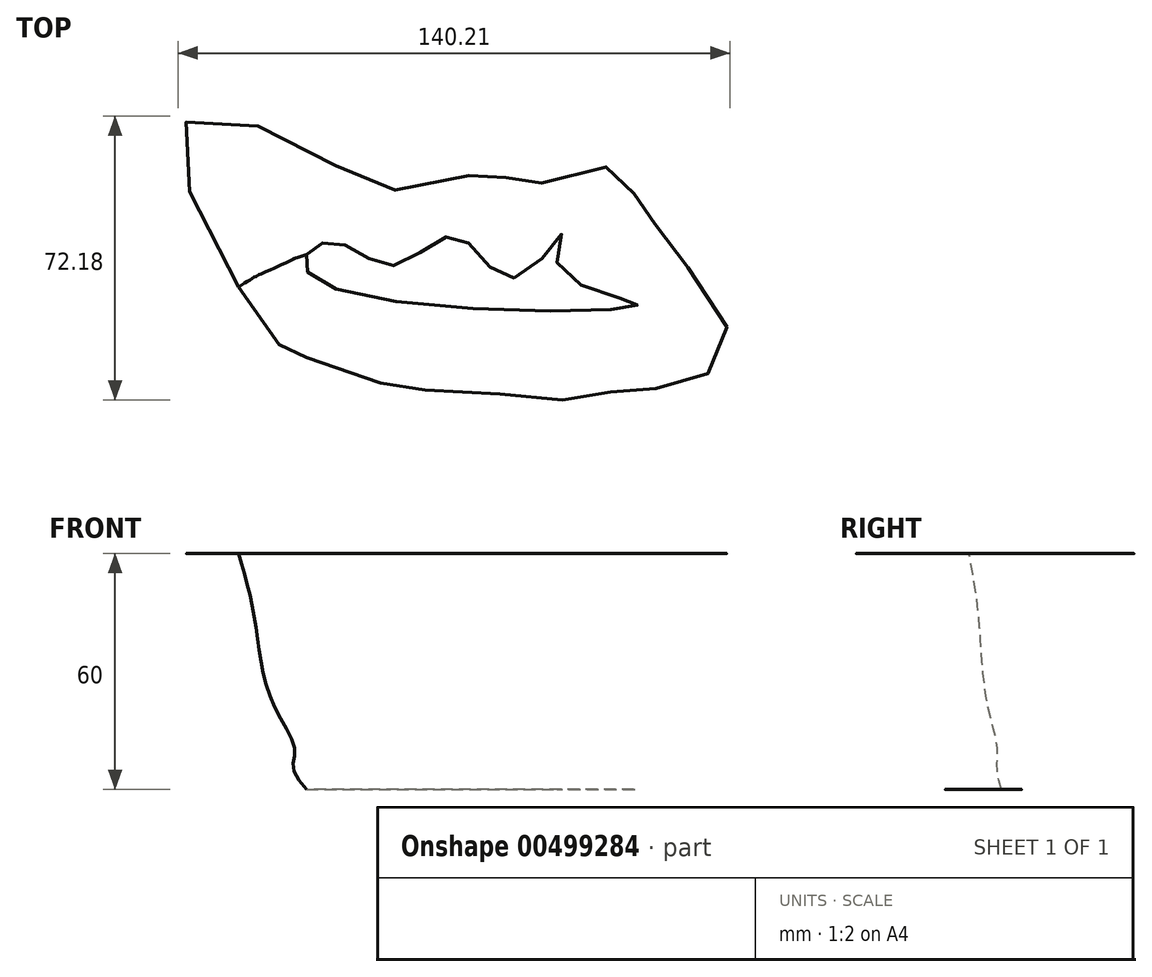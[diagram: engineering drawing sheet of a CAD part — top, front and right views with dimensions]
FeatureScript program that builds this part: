
annotation { "Feature Type Name" : "Feature", "Feature Type Description" : "" }
export const myFeature = defineFeature(function(context is Context, id is Id, definition is map)
    precondition{}
    {
        {
            var Q0;
            Q0=qCreatedBy(makeId("Top.planeOp"),FACE);
            var sketch = newSketch(context, id + "F0", { "sketchPlane" : qUnion([Q0])});
            skFitSpline(sketch, "E0", {"points": [v(-38.2, 16.28) * mm, v(-29.92, 19.29) * mm, v(-16, 13.45) * mm, v(0, 20.98) * mm, v(13.92, 10.26) * mm, v(27.28, 22.3) * mm, v(25.97, 12.89) * mm, v(45.91, 3.48) * mm, v(-31.61, 7.8) * mm, v(-38.2, 16.28) * mm]});
            skSolve(sketch);
        }
        {
            var Q0;
            Q0=makeQuery(id+"F0.imprint","IMPRINT",FACE,{"disambiguationData":[TD([[makeQuery(id+"F0.imprint","IMPRINT",EDGE,{"derivedFrom":sQuery(id+"F0.wireOp",EDGE,"E0")}),-1.0]])]});
            cPlane(context, id + "F1", {"entities" : qUnion([Q0]), "cplaneType" : CPlaneType.OFFSET, "offset" : 5 * mm, "width" : 150 * mm, "height" : 150 * mm});
        }
        {
            var Q0;
            Q0=qCreatedBy(id+"F1.planeOp",FACE);
            var sketch = newSketch(context, id + "F2", { "sketchPlane" : qUnion([Q0])});
            skFitSpline(sketch, "E1", {"points": [v(48.17, 4.42) * mm, v(30.67, 11) * mm, v(32.74, 26.25) * mm, v(14.3, 14.2) * mm, v(4.33, 24.18) * mm, v(-11.3, 21.17) * mm, v(-19.2, 16.84) * mm, v(-35, 23.24) * mm, v(-41.96, 17.6) * mm, v(-33.5, 3.86) * mm, v(-30.48, 3.3) * mm, v(41.59, -2.54) * mm, v(48.17, 4.42) * mm]});
            skSolve(sketch);
        }
        {
            var Q0;
            Q0=makeQuery(id+"F2.imprint","IMPRINT",FACE,{"disambiguationData":[TD([[makeQuery(id+"F2.imprint","IMPRINT",EDGE,{"derivedFrom":sQuery(id+"F2.wireOp",EDGE,"E1")}),1.0]])]});
            cPlane(context, id + "F3", {"entities" : qUnion([Q0]), "cplaneType" : CPlaneType.OFFSET, "offset" : 5 * mm, "width" : 150 * mm, "height" : 150 * mm});
        }
        {
            var Q0;
            Q0=qCreatedBy(id+"F3.planeOp",FACE);
            var sketch = newSketch(context, id + "F4", { "sketchPlane" : qUnion([Q0])});
            skFitSpline(sketch, "E2", {"points": [v(-33.3, 4.23) * mm, v(-41.2, 18.53) * mm, v(-29.17, 21.73) * mm, v(-17.69, 16.84) * mm, v(4.14, 18.91) * mm, v(14.11, 12.14) * mm, v(30.48, 21.92) * mm, v(29.35, 11.38) * mm, v(46.1, 4.8) * mm, v(31.42, -5.74) * mm, v(-25.4, 1.79) * mm, v(-33.3, 4.23) * mm]});
            skSolve(sketch);
        }
        {
            var Q0;
            Q0=makeQuery(id+"F4.imprint","IMPRINT",FACE,{"disambiguationData":[TD([[makeQuery(id+"F4.imprint","IMPRINT",EDGE,{"derivedFrom":sQuery(id+"F4.wireOp",EDGE,"E2")}),-1.0]])]});
            cPlane(context, id + "F5", {"entities" : qUnion([Q0]), "cplaneType" : CPlaneType.OFFSET, "offset" : 10 * mm, "width" : 150 * mm, "height" : 150 * mm});
        }
        {
            var Q0;
            Q0=qCreatedBy(id+"F5.planeOp",FACE);
            var sketch = newSketch(context, id + "F6", { "sketchPlane" : qUnion([Q0])});
            skFitSpline(sketch, "E3", {"points": [v(-38.58, 2.92) * mm, v(-47.42, 27.38) * mm, v(-18.25, 18.72) * mm, v(3.95, 25.3) * mm, v(18.63, 17.22) * mm, v(31.24, 24.37) * mm, v(36.7, 12.51) * mm, v(51.94, 0) * mm, v(33.68, -9.7) * mm, v(5.46, -7.24) * mm, v(-16, -2.54) * mm, v(-19.76, -2.35) * mm, v(-38.58, 2.92) * mm]});
            skSolve(sketch);
        }
        {
            var Q0;
            Q0=makeQuery(id+"F6.imprint","IMPRINT",FACE,{"disambiguationData":[TD([[makeQuery(id+"F6.imprint","IMPRINT",EDGE,{"derivedFrom":sQuery(id+"F6.wireOp",EDGE,"E3")}),-1.0]])]});
            cPlane(context, id + "F7", {"entities" : qUnion([Q0]), "cplaneType" : CPlaneType.OFFSET, "offset" : 25 * mm, "width" : 150 * mm, "height" : 150 * mm});
        }
        {
            var Q0;
            Q0=qCreatedBy(id+"F7.planeOp",FACE);
            var sketch = newSketch(context, id + "F8", { "sketchPlane" : qUnion([Q0])});
            skFitSpline(sketch, "E4", {"points": [v(-47.8, 2.54) * mm, v(-61.34, 42.8) * mm, v(-21.08, 25.69) * mm, v(6.96, 31.52) * mm, v(17.88, 24.56) * mm, v(32.18, 31.14) * mm, v(34.62, 29.64) * mm, v(42.72, 22.3) * mm, v(44.97, 16.65) * mm, v(58.15, -1.41) * mm, v(50.24, -10.07) * mm, v(25.4, -14.77) * mm, v(-2.63, -8.75) * mm, v(-6.2, -8.94) * mm, v(-28.8, -6.68) * mm, v(-32.37, -6.5) * mm, v(-45.35, 0) * mm, v(-47.8, 2.54) * mm]});
            skSolve(sketch);
        }
        {
            var Q0;
            Q0=makeQuery(id+"F8.imprint","IMPRINT",FACE,{"disambiguationData":[TD([[makeQuery(id+"F8.imprint","IMPRINT",EDGE,{"derivedFrom":sQuery(id+"F8.wireOp",EDGE,"E4")}),-1.0]])]});
            cPlane(context, id + "F9", {"entities" : qUnion([Q0]), "cplaneType" : CPlaneType.OFFSET, "offset" : 15 * mm, "width" : 150 * mm, "height" : 150 * mm});
        }
        {
            var Q0;
            Q0=qCreatedBy(id+"F9.planeOp",FACE);
            var sketch = newSketch(context, id + "F10", { "sketchPlane" : qUnion([Q0])});
            skFitSpline(sketch, "E5", {"points": [v(-55.56, 8.19) * mm, v(-69.48, 49.2) * mm, v(-38.81, 43.75) * mm, v(-15.29, 32.65) * mm, v(9.74, 37.54) * mm, v(12.56, 35.66) * mm, v(14.44, 33.59) * mm, v(37.21, 38.48) * mm, v(40.22, 37.16) * mm, v(49.07, 26.81) * mm, v(50.57, 23.62) * mm, v(62.99, 7.43) * mm, v(68.26, -10.26) * mm, v(51.7, -17.78) * mm, v(47.94, -17.6) * mm, v(28.37, -20.42) * mm, v(25.54, -20.6) * mm, v(-6.45, -17.97) * mm, v(-12.84, -18.16) * mm, v(-39.56, -9.5) * mm, v(-43.14, -8.37) * mm, v(-55.56, 8.19) * mm]});
            skSolve(sketch);
        }
        {
            var Q0;
            Q0=makeQuery(id+"F0.imprint","IMPRINT",FACE,{"disambiguationData":[TD([[makeQuery(id+"F0.imprint","IMPRINT",EDGE,{"derivedFrom":sQuery(id+"F0.wireOp",EDGE,"E0")}),-1.0]])]});
            var Q1;
            Q1=makeQuery(id+"F2.imprint","IMPRINT",FACE,{"disambiguationData":[TD([[makeQuery(id+"F2.imprint","IMPRINT",EDGE,{"derivedFrom":sQuery(id+"F2.wireOp",EDGE,"E1")}),1.0]])]});
            var Q2;
            Q2=makeQuery(id+"F4.imprint","IMPRINT",FACE,{"disambiguationData":[TD([[makeQuery(id+"F4.imprint","IMPRINT",EDGE,{"derivedFrom":sQuery(id+"F4.wireOp",EDGE,"E2")}),-1.0]])]});
            var Q3;
            Q3=makeQuery(id+"F6.imprint","IMPRINT",FACE,{"disambiguationData":[TD([[makeQuery(id+"F6.imprint","IMPRINT",EDGE,{"derivedFrom":sQuery(id+"F6.wireOp",EDGE,"E3")}),-1.0]])]});
            var Q4;
            Q4=makeQuery(id+"F8.imprint","IMPRINT",FACE,{"disambiguationData":[TD([[makeQuery(id+"F8.imprint","IMPRINT",EDGE,{"derivedFrom":sQuery(id+"F8.wireOp",EDGE,"E4")}),-1.0]])]});
            var Q5;
            Q5=makeQuery(id+"F10.imprint","IMPRINT",FACE,{"disambiguationData":[TD([[makeQuery(id+"F10.imprint","IMPRINT",EDGE,{"derivedFrom":sQuery(id+"F10.wireOp",EDGE,"E5")}),-1.0]])]});
            loft(context, id + "F11", {"sheetProfilesArray" : [{ "sheetProfileEntities" : qUnion([Q0]) }, { "sheetProfileEntities" : qUnion([Q1]) }, { "sheetProfileEntities" : qUnion([Q2]) }, { "sheetProfileEntities" : qUnion([Q3]) }, { "sheetProfileEntities" : qUnion([Q4]) }, { "sheetProfileEntities" : qUnion([Q5]) }]});
        }
    });
